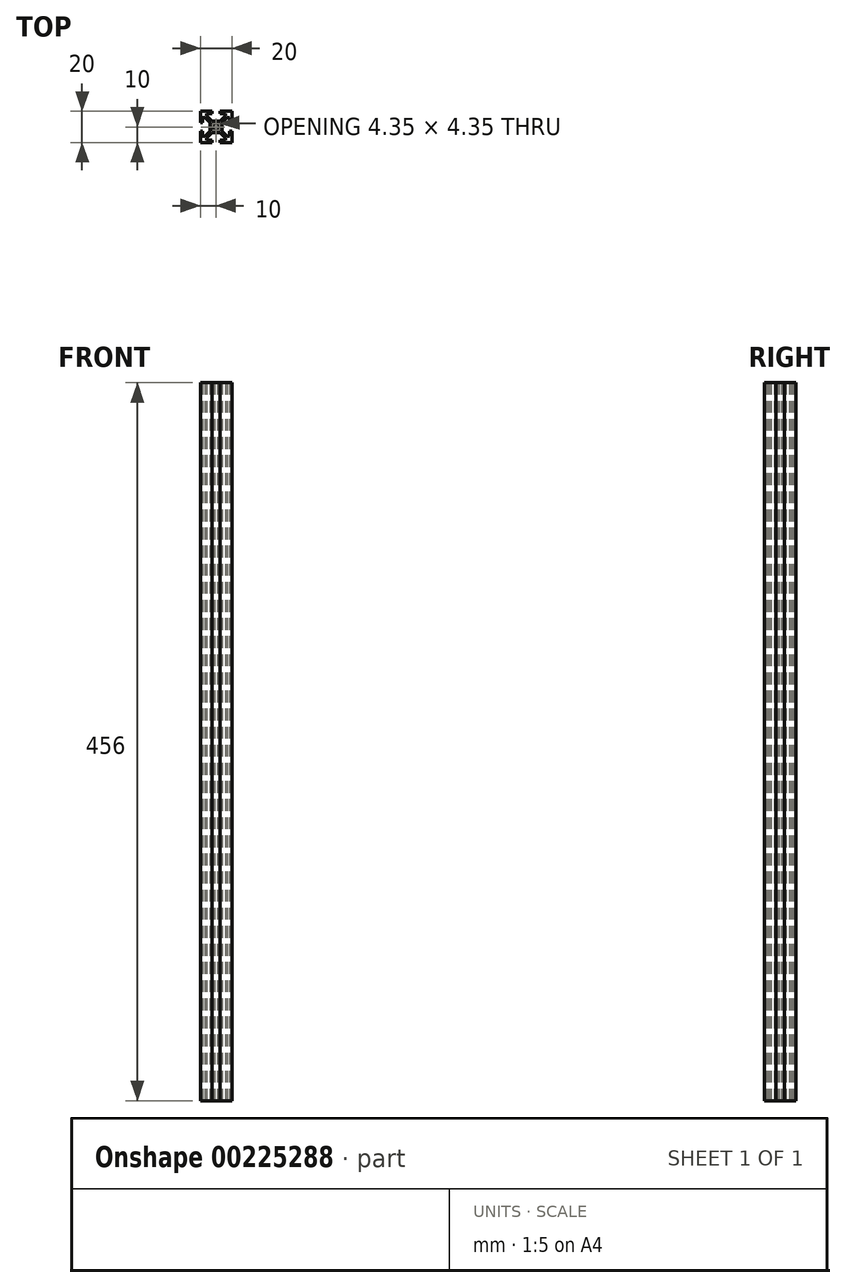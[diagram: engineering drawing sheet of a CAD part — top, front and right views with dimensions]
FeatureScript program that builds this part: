
annotation { "Feature Type Name" : "Feature", "Feature Type Description" : "" }
export const myFeature = defineFeature(function(context is Context, id is Id, definition is map)
    precondition{}
    {
        {
            var Q0;
            Q0=qCreatedBy(makeId("Top.planeOp"),FACE);
            var sketch = newSketch(context, id + "F0", { "sketchPlane" : qUnion([Q0])});
            skLineSegment(sketch, "E0.bottom", {"start": v(10, 10) * mm, "end": v(-10, 10) * mm});
            skLineSegment(sketch, "E0.top", {"start": v(10, -10) * mm, "end": v(-10, -10) * mm});
            skLineSegment(sketch, "E0.left", {"start": v(10, 10) * mm, "end": v(10, -10) * mm});
            skLineSegment(sketch, "E0.right", {"start": v(-10, 10) * mm, "end": v(-10, -10) * mm});
            skPoint(sketch, "E0.middle", {"position": v(0, 0) * mm});
            skLineSegment(sketch, "E1", {"start": v(-10, 10) * mm, "end": v(10, -10) * mm, "construction": true});
            skLineSegment(sketch, "E2", {"start": v(-10, -10) * mm, "end": v(10, 10) * mm, "construction": true});
            skLineSegment(sketch, "E3", {"start": v(0, 10) * mm, "end": v(0, -10) * mm, "construction": true});
            skLineSegment(sketch, "E4", {"start": v(-10, 0) * mm, "end": v(10, 0) * mm, "construction": true});
            skPoint(sketch, "E4.endSnap0", {"position": v(10, 0) * mm});
            skLineSegment(sketch, "E5", {"start": v(-2.63, 13.49) * mm, "end": v(2.63, 13.49) * mm});
            skLineSegment(sketch, "E6", {"start": v(2.63, 13.49) * mm, "end": v(2.63, 8.5) * mm});
            skLineSegment(sketch, "E7", {"start": v(2.63, 8.5) * mm, "end": v(6, 8.5) * mm});
            skLineSegment(sketch, "E8", {"start": v(6, 8.5) * mm, "end": v(6, 7.06) * mm});
            skLineSegment(sketch, "E9", {"start": v(6, 7.06) * mm, "end": v(2.6, 3.66) * mm});
            skLineSegment(sketch, "E10", {"start": v(2.6, 3.66) * mm, "end": v(-2.6, 3.66) * mm});
            skLineSegment(sketch, "E11", {"start": v(-2.6, 3.66) * mm, "end": v(-6, 7.06) * mm});
            skLineSegment(sketch, "E12", {"start": v(-6, 7.06) * mm, "end": v(-6, 8.5) * mm});
            skLineSegment(sketch, "E13", {"start": v(-6, 8.5) * mm, "end": v(-2.63, 8.5) * mm});
            skLineSegment(sketch, "E14", {"start": v(-2.63, 8.5) * mm, "end": v(-2.63, 13.49) * mm});
            skCircle(sketch, "E15", {"center": v(0, 0) * mm, "radius": 2.1 * mm});
            skLineSegment(sketch, "E16.MirrorCS", {"start": v(-7.06, 6) * mm, "end": v(-8.5, 6) * mm});
            skLineSegment(sketch, "E17.MirrorCS", {"start": v(-3.66, 2.6) * mm, "end": v(-7.06, 6) * mm});
            skLineSegment(sketch, "E18.MirrorCS", {"start": v(-8.5, 6) * mm, "end": v(-8.5, 2.63) * mm});
            skLineSegment(sketch, "E19.MirrorCS", {"start": v(-3.66, -2.6) * mm, "end": v(-3.66, 2.6) * mm});
            skLineSegment(sketch, "E20.MirrorCS", {"start": v(-7.06, -6) * mm, "end": v(-3.66, -2.6) * mm});
            skLineSegment(sketch, "E21.MirrorCS", {"start": v(-8.5, -6) * mm, "end": v(-7.06, -6) * mm});
            skLineSegment(sketch, "E22.MirrorCS", {"start": v(-8.5, -2.63) * mm, "end": v(-8.5, -6) * mm});
            skLineSegment(sketch, "E23.MirrorCS", {"start": v(-13.49, -2.63) * mm, "end": v(-8.5, -2.63) * mm});
            skLineSegment(sketch, "E24.MirrorCS", {"start": v(-13.49, 2.63) * mm, "end": v(-13.49, -2.63) * mm});
            skLineSegment(sketch, "E25.MirrorCS", {"start": v(-8.5, 2.63) * mm, "end": v(-13.49, 2.63) * mm});
            skLineSegment(sketch, "E26.MirrorCS", {"start": v(-2.6, -3.66) * mm, "end": v(-6, -7.06) * mm});
            skLineSegment(sketch, "E27.MirrorCS", {"start": v(2.6, -3.66) * mm, "end": v(-2.6, -3.66) * mm});
            skLineSegment(sketch, "E28.MirrorCS", {"start": v(6, -7.06) * mm, "end": v(2.6, -3.66) * mm});
            skLineSegment(sketch, "E29.MirrorCS", {"start": v(6, -8.5) * mm, "end": v(6, -7.06) * mm});
            skLineSegment(sketch, "E30.MirrorCS", {"start": v(2.63, -8.5) * mm, "end": v(6, -8.5) * mm});
            skLineSegment(sketch, "E31.MirrorCS", {"start": v(2.63, -13.49) * mm, "end": v(2.63, -8.5) * mm});
            skLineSegment(sketch, "E32.MirrorCS", {"start": v(-2.63, -13.49) * mm, "end": v(2.63, -13.49) * mm});
            skLineSegment(sketch, "E33.MirrorCS", {"start": v(-2.63, -8.5) * mm, "end": v(-2.63, -13.49) * mm});
            skLineSegment(sketch, "E34.MirrorCS", {"start": v(-6, -8.5) * mm, "end": v(-2.63, -8.5) * mm});
            skLineSegment(sketch, "E35.MirrorCS", {"start": v(-6, -7.06) * mm, "end": v(-6, -8.5) * mm});
            skLineSegment(sketch, "E36.MirrorCS", {"start": v(7.06, 6) * mm, "end": v(3.66, 2.6) * mm});
            skLineSegment(sketch, "E37.MirrorCS", {"start": v(8.5, 6) * mm, "end": v(7.06, 6) * mm});
            skLineSegment(sketch, "E38.MirrorCS", {"start": v(8.5, 2.63) * mm, "end": v(8.5, 6) * mm});
            skLineSegment(sketch, "E39.MirrorCS", {"start": v(13.49, 2.63) * mm, "end": v(8.5, 2.63) * mm});
            skLineSegment(sketch, "E40.MirrorCS", {"start": v(13.49, -2.63) * mm, "end": v(13.49, 2.63) * mm});
            skLineSegment(sketch, "E41.MirrorCS", {"start": v(8.5, -2.63) * mm, "end": v(13.49, -2.63) * mm});
            skLineSegment(sketch, "E42.MirrorCS", {"start": v(8.5, -6) * mm, "end": v(8.5, -2.63) * mm});
            skLineSegment(sketch, "E43.MirrorCS", {"start": v(7.06, -6) * mm, "end": v(8.5, -6) * mm});
            skLineSegment(sketch, "E44.MirrorCS", {"start": v(3.66, -2.6) * mm, "end": v(7.06, -6) * mm});
            skLineSegment(sketch, "E45.MirrorCS", {"start": v(3.66, 2.6) * mm, "end": v(3.66, -2.6) * mm});
            skCircle(sketch, "E46", {"center": v(-1.48, 1.48) * mm, "radius": 0.7 * mm});
            skCircle(sketch, "E47.MirrorC", {"center": v(1.48, 1.48) * mm, "radius": 0.7 * mm});
            skCircle(sketch, "E48.MirrorC", {"center": v(-1.48, -1.48) * mm, "radius": 0.7 * mm});
            skCircle(sketch, "E49.MirrorC", {"center": v(1.48, -1.48) * mm, "radius": 0.7 * mm});
            skSolve(sketch);
        }
        {
            var Q0;
            {var subQ29=sQuery(id+"F0.wireOp",EDGE,"E7");Q0=makeQuery(id+"F0.imprint","IMPRINT",FACE,{"disambiguationData":[TD([[makeQuery(id+"F0.imprint","IMPRINT",EDGE,{"derivedFrom":subQ29}),1.0]])]});}
            extrude(context, id + "F1", {"entities" : qUnion([Q0]), "depth" : 456 * mm});
        }
    });
